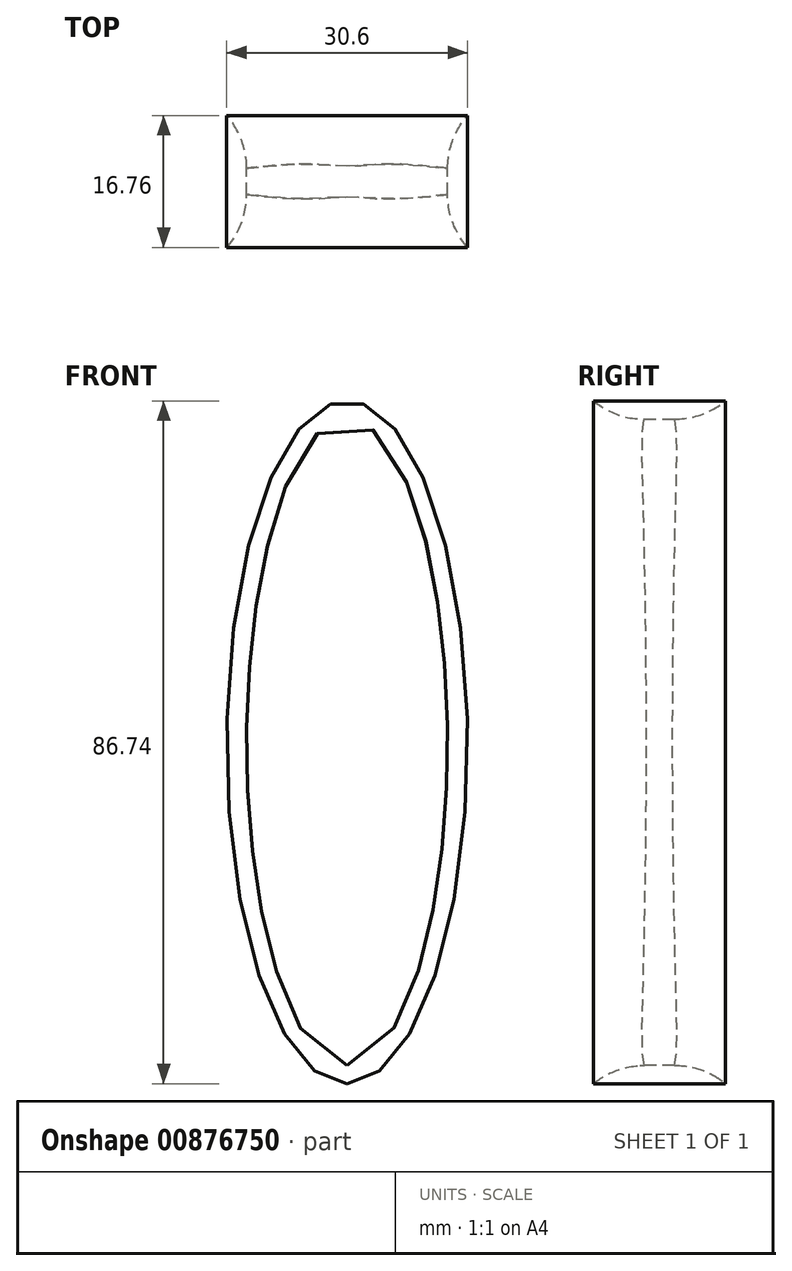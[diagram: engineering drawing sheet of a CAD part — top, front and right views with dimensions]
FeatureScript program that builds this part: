
annotation { "Feature Type Name" : "Feature", "Feature Type Description" : "" }
export const myFeature = defineFeature(function(context is Context, id is Id, definition is map)
    precondition{}
    {
        {
            var Q0;
            Q0=qCreatedBy(makeId("Front.planeOp"),FACE);
            var sketch = newSketch(context, id + "F0", { "sketchPlane" : qUnion([Q0])});
            skEllipse(sketch, "E0", {"center": v(0, 0) * mm, "majorRadius": 43.37 * mm, "minorRadius": 15.3 * mm, "majorAxis": v(0, -1)});
            skSolve(sketch);
        }
        {
            var Q0;
            Q0 = qSketchRegion(id + "F0", true);
            extrude(context, id + "F1", {"entities" : qUnion([Q0]), "depth" : 16.76 * mm, "offsetDistance" : 25.4 * mm});
        }
        {
            var Q0;
            Q0=makeQuery(id+"F1.opExtrude","CAP_FACE",FACE,{"disambiguationData":[OSD([sQuery(id+"F0.wireOp",EDGE,"E0")])],"isStart":false});
            var sketch = newSketch(context, id + "F2", { "sketchPlane" : qUnion([Q0])});
            skEllipse(sketch, "E1", {"center": v(0, 0) * mm, "majorRadius": 41.05 * mm, "minorRadius": 12.76 * mm, "majorAxis": v(0, -1)});
            skSolve(sketch);
        }
        {
            var Q0;
            Q0=makeQuery(id+"F2.imprint","IMPRINT",FACE,{"disambiguationData":[TD([[makeQuery(id+"F2.imprint","IMPRINT",EDGE,{"derivedFrom":sQuery(id+"F2.wireOp",EDGE,"E1")}),1.0]])]});
            extrude(context, id + "F3", {"entities" : qUnion([Q0]), "operationType" : NewBodyOperationType.REMOVE, "oppositeDirection" : true, "depth" : 25.4 * mm, "offsetDistance" : 25.4 * mm});
        }
        {
            var Q0;
            Q0=makeQuery(id+"F3.boolean.opBoolean","COPY",FACE,{"derivedFrom":makeQuery(id+"F3.opExtrude","SWEPT_FACE",FACE,{"disambiguationData":[OSD([sQuery(id+"F2.wireOp",EDGE,"E1")])]})});
            fillet(context, id + "F4", {"entities" : qUnion([Q0]), "radius" : 10.16 * mm, "tangentPropagation" : true, "allowEdgeOverflow" : false});
        }
    });
